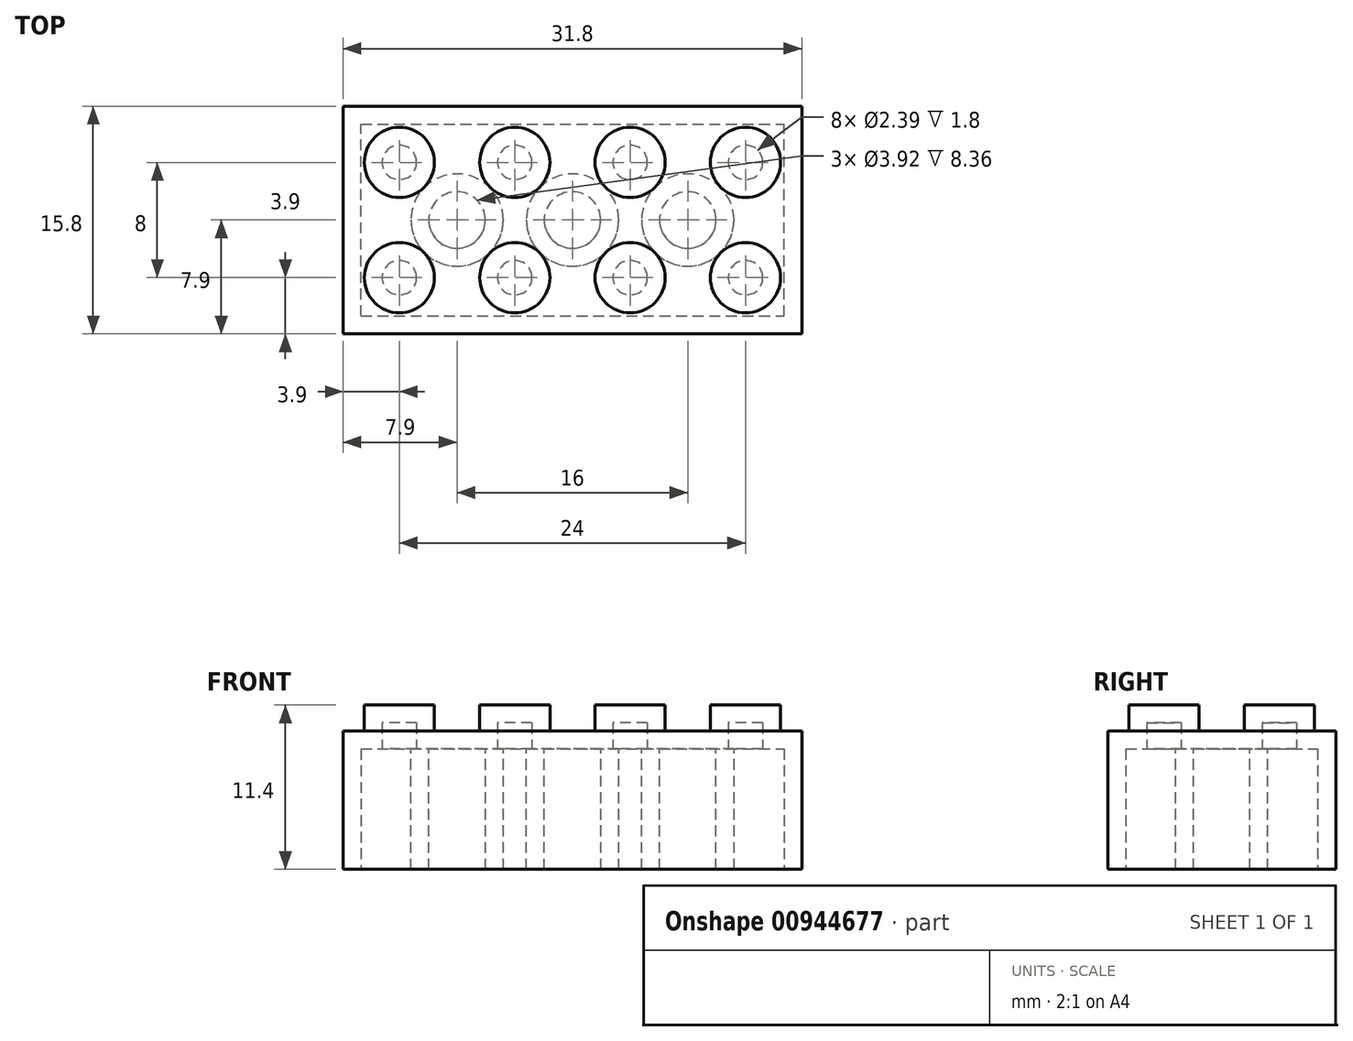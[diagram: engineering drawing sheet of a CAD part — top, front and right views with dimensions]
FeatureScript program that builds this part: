
annotation { "Feature Type Name" : "Feature", "Feature Type Description" : "" }
export const myFeature = defineFeature(function(context is Context, id is Id, definition is map)
    precondition{}
    {
        {
            var Q0;
            Q0=qCreatedBy(makeId("Top.planeOp"),FACE);
            var sketch = newSketch(context, id + "F0", { "sketchPlane" : qUnion([Q0])});
            skLineSegment(sketch, "E0.bottom", {"start": v(0, 0) * mm, "end": v(31.8, 0) * mm});
            skLineSegment(sketch, "E0.top", {"start": v(0, 15.8) * mm, "end": v(31.8, 15.8) * mm});
            skLineSegment(sketch, "E0.left", {"start": v(0, 0) * mm, "end": v(0, 15.8) * mm});
            skLineSegment(sketch, "E0.right", {"start": v(31.8, 0) * mm, "end": v(31.8, 15.8) * mm});
            skSolve(sketch);
        }
        {
            var Q0;
            Q0=makeQuery(id+"F0.imprint","IMPRINT",FACE,{"disambiguationData":[TD([[makeQuery(id+"F0.imprint","IMPRINT",EDGE,{"derivedFrom":sQuery(id+"F0.wireOp",EDGE,"E0.bottom")}),1.0]])]});
            extrude(context, id + "F1", {"entities" : qUnion([Q0]), "depth" : 9.6 * mm, "offsetDistance" : 25 * mm});
        }
        {
            var Q0;
            Q0=makeQuery(id+"F1.opExtrude","CAP_FACE",FACE,{"disambiguationData":[OSD([sQuery(id+"F0.wireOp",EDGE,"E0.bottom"),sQuery(id+"F0.wireOp",EDGE,"E0.top"),sQuery(id+"F0.wireOp",EDGE,"E0.left"),sQuery(id+"F0.wireOp",EDGE,"E0.right")])],"isStart":false});
            var sketch = newSketch(context, id + "F2", { "sketchPlane" : qUnion([Q0])});
            skLineSegment(sketch, "E1", {"start": v(0, 7.9) * mm, "end": v(31.8, 7.9) * mm, "construction": true});
            skLineSegment(sketch, "E2", {"start": v(15.9, 15.8) * mm, "end": v(15.9, 0) * mm, "construction": true});
            skLineSegment(sketch, "E3", {"start": v(0, 11.9) * mm, "end": v(31.8, 11.9) * mm, "construction": true});
            skLineSegment(sketch, "E4", {"start": v(0, 3.9) * mm, "end": v(31.8, 3.9) * mm, "construction": true});
            skPoint(sketch, "E5", {"position": v(3.9, 11.9) * mm});
            skPoint(sketch, "E6", {"position": v(11.9, 11.9) * mm});
            skPoint(sketch, "E7", {"position": v(19.9, 11.9) * mm});
            skPoint(sketch, "E8", {"position": v(27.9, 11.9) * mm});
            skPoint(sketch, "E9", {"position": v(3.9, 3.9) * mm});
            skPoint(sketch, "E10", {"position": v(11.9, 3.9) * mm});
            skPoint(sketch, "E11", {"position": v(19.9, 3.9) * mm});
            skPoint(sketch, "E12", {"position": v(27.9, 3.9) * mm});
            skCircle(sketch, "E13", {"center": v(3.9, 11.9) * mm, "radius": 2.44 * mm});
            skCircle(sketch, "E14", {"center": v(11.9, 11.9) * mm, "radius": 2.44 * mm});
            skCircle(sketch, "E15", {"center": v(19.9, 11.9) * mm, "radius": 2.44 * mm});
            skCircle(sketch, "E16", {"center": v(27.9, 11.9) * mm, "radius": 2.44 * mm});
            skCircle(sketch, "E17", {"center": v(27.9, 3.9) * mm, "radius": 2.44 * mm});
            skCircle(sketch, "E18", {"center": v(19.9, 3.9) * mm, "radius": 2.44 * mm});
            skCircle(sketch, "E19", {"center": v(11.9, 3.9) * mm, "radius": 2.44 * mm});
            skCircle(sketch, "E20", {"center": v(3.9, 3.9) * mm, "radius": 2.44 * mm});
            skSolve(sketch);
        }
        {
            var Q0;
            Q0 = qSketchRegion(id + "F2", true);
            extrude(context, id + "F3", {"entities" : qUnion([Q0]), "operationType" : NewBodyOperationType.ADD, "depth" : 1.8 * mm, "offsetDistance" : 25 * mm});
        }
        {
            var Q0;
            Q0=makeQuery(id+"F1.opExtrude","CAP_FACE",FACE,{"disambiguationData":[OSD([sQuery(id+"F0.wireOp",EDGE,"E0.bottom"),sQuery(id+"F0.wireOp",EDGE,"E0.top"),sQuery(id+"F0.wireOp",EDGE,"E0.left"),sQuery(id+"F0.wireOp",EDGE,"E0.right")])],"isStart":true});
            shell(context, id + "F4", {"entities" : qUnion([Q0]), "thickness" : 1.24 * mm});
        }
        {
            var Q0;
            Q0=makeQuery(id+"F4.opShell","OFFSET_FACE",FACE,{"disambiguationData":[OSD([sQuery(id+"F0.wireOp",EDGE,"E0.bottom"),sQuery(id+"F0.wireOp",EDGE,"E0.top"),sQuery(id+"F0.wireOp",EDGE,"E0.left"),sQuery(id+"F0.wireOp",EDGE,"E0.right")])]});
            var sketch = newSketch(context, id + "F5", { "sketchPlane" : qUnion([Q0])});
            skLineSegment(sketch, "E21", {"start": v(1.24, -7.9) * mm, "end": v(30.56, -7.9) * mm, "construction": true});
            skLineSegment(sketch, "E22", {"start": v(15.9, -1.24) * mm, "end": v(15.9, -14.56) * mm, "construction": true});
            skCircle(sketch, "E23", {"center": v(15.9, -7.9) * mm, "radius": 3.2 * mm});
            skCircle(sketch, "E24", {"center": v(7.9, -7.9) * mm, "radius": 3.2 * mm});
            skCircle(sketch, "E25", {"center": v(23.9, -7.9) * mm, "radius": 3.2 * mm});
            skSolve(sketch);
        }
        {
            var Q0;
            Q0=makeQuery(id+"F5.imprint","IMPRINT",FACE,{"disambiguationData":[TD([[makeQuery(id+"F5.imprint","IMPRINT",EDGE,{"derivedFrom":sQuery(id+"F5.wireOp",EDGE,"E24")}),1.0]])]});
            var Q1;
            Q1=makeQuery(id+"F5.imprint","IMPRINT",FACE,{"disambiguationData":[TD([[makeQuery(id+"F5.imprint","IMPRINT",EDGE,{"derivedFrom":sQuery(id+"F5.wireOp",EDGE,"E23")}),1.0]])]});
            var Q2;
            Q2=makeQuery(id+"F5.imprint","IMPRINT",FACE,{"disambiguationData":[TD([[makeQuery(id+"F5.imprint","IMPRINT",EDGE,{"derivedFrom":sQuery(id+"F5.wireOp",EDGE,"E25")}),1.0]])]});
            extrude(context, id + "F6", {"entities" : qUnion([Q0, Q1, Q2]), "operationType" : NewBodyOperationType.ADD, "depth" : (9.6 - 1.24) * mm, "offsetDistance" : 25 * mm});
        }
        {
            var Q0;
            Q0=makeQuery(id+"F6.opExtrude","CAP_FACE",FACE,{"disambiguationData":[OSD([sQuery(id+"F5.wireOp",EDGE,"E25")])],"isStart":false});
            var Q1;
            Q1=makeQuery(id+"F6.opExtrude","CAP_FACE",FACE,{"disambiguationData":[OSD([sQuery(id+"F5.wireOp",EDGE,"E23")])],"isStart":false});
            var Q2;
            Q2=makeQuery(id+"F6.opExtrude","CAP_FACE",FACE,{"disambiguationData":[OSD([sQuery(id+"F5.wireOp",EDGE,"E24")])],"isStart":false});
            shell(context, id + "F7", {"entities" : qUnion([Q0, Q1, Q2]), "thickness" : 1.24 * mm});
        }
    });
